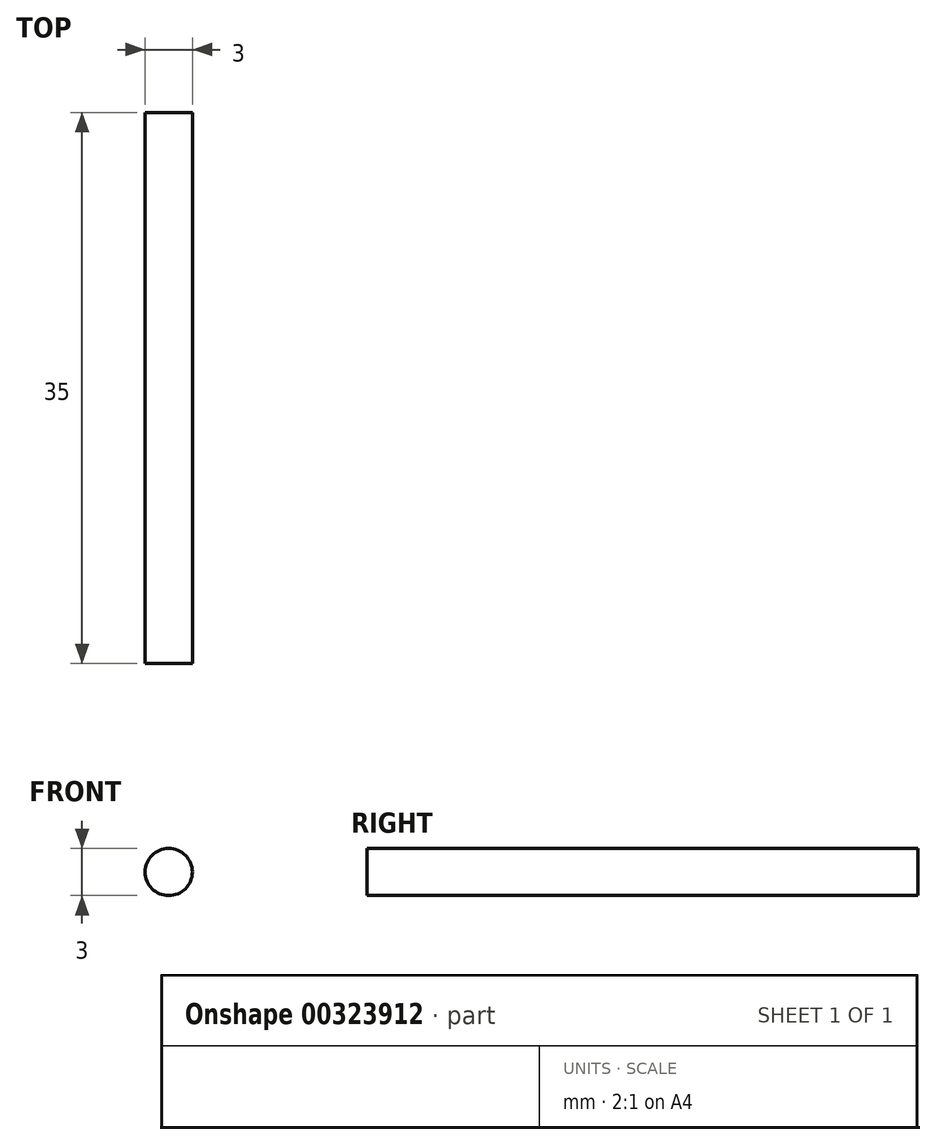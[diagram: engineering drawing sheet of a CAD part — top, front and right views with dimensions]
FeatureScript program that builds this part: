
annotation { "Feature Type Name" : "Feature", "Feature Type Description" : "" }
export const myFeature = defineFeature(function(context is Context, id is Id, definition is map)
    precondition{}
    {
        {
            var Q0;
            Q0=qCreatedBy(makeId("Front.planeOp"),FACE);
            var sketch = newSketch(context, id + "F0", { "sketchPlane" : qUnion([Q0])});
            skCircle(sketch, "E0", {"center": v(0, 0) * mm, "radius": 1.5 * mm});
            skSolve(sketch);
        }
        {
            var Q0;
            Q0=makeQuery(id+"F0.imprint","IMPRINT",FACE,{"disambiguationData":[TD([[makeQuery(id+"F0.imprint","IMPRINT",EDGE,{"derivedFrom":sQuery(id+"F0.wireOp",EDGE,"E0")}),1.0]])]});
            extrude(context, id + "F1", {"entities" : qUnion([Q0]), "depth" : 35 * mm});
        }
    });
